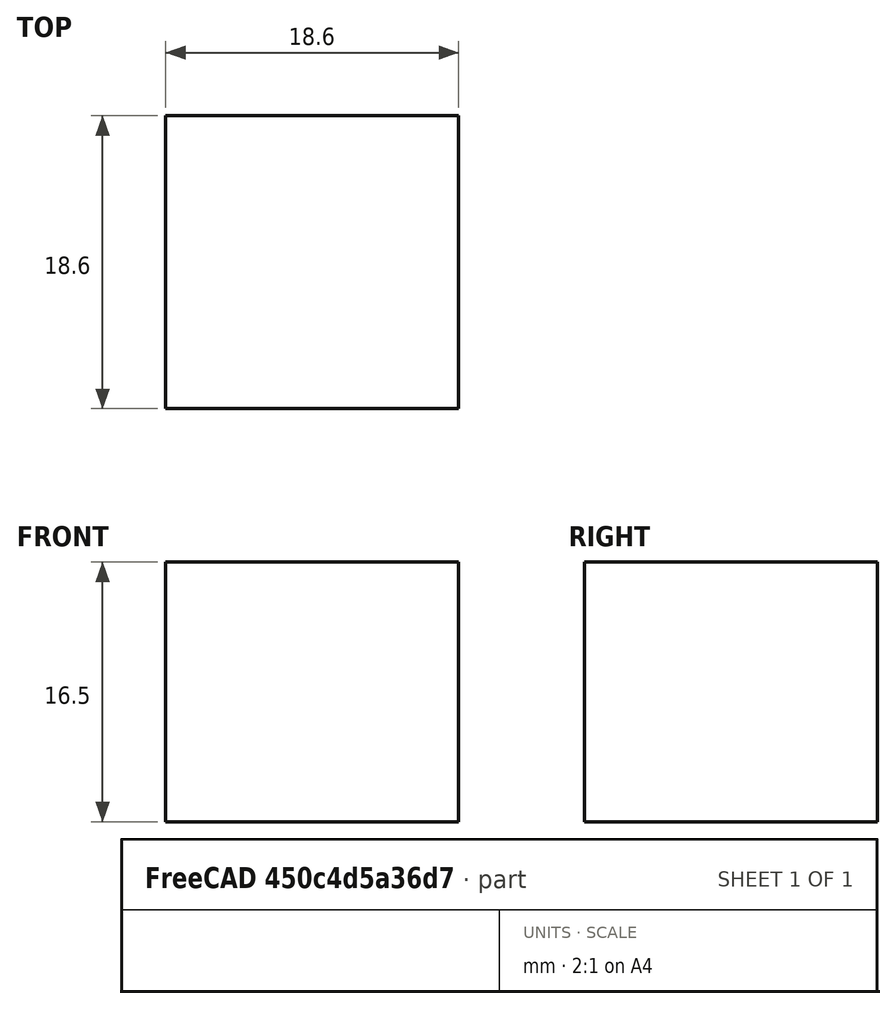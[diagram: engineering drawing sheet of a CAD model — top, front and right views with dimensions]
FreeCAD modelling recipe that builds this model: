
FCSTD DOCUMENT  (FreeCAD 0.15R4671 (Git))
Label: Notched Center Square
License: All rights reserved
LicenseURL: http://en.wikipedia.org/wiki/All_rights_reserved
objects: Sketcher::SketchObject×2, PartDesign::Pad×1
note: 4 computed .brp shape members not serialized (recipe doc carries the construction recipe); baked Part::Feature solids carry a one-line shape summary decoded from their .brp

FEATURE [Sketcher::SketchObject] Sketch
  sketch-geometry (4):
    g0: LineSegment StartX=-9.3 StartY=9.3 StartZ=0 EndX=9.3 EndY=9.3 EndZ=0
    g1: LineSegment StartX=9.3 StartY=9.3 StartZ=0 EndX=9.3 EndY=-9.3 EndZ=0
    g2: LineSegment StartX=9.3 StartY=-9.3 StartZ=0 EndX=-9.3 EndY=-9.3 EndZ=0
    g3: LineSegment StartX=-9.3 StartY=-9.3 StartZ=0 EndX=-9.3 EndY=9.3 EndZ=0
  constraints (12):
    c: Coincident(g0,g1)
    c: Coincident(g1,g2)
    c: Coincident(g2,g3)
    c: Coincident(g3,g0)
    c: Horizontal(g0)
    c: Horizontal(g2)
    c: Vertical(g1)
    c: Vertical(g3)
    c: Symmetric(g0,g0,g-2)
    c: Symmetric(g0,g2,g-1)
    c: Equal(g3,g0)
    c: Distance(g0) = 18.6
FEATURE [PartDesign::Pad] Pad
  Length = 16.5
  Length2 = 100
  Sketch = -> Sketch
  Type = 0
FEATURE [Sketcher::SketchObject] Sketch001
  ExternalGeometry = -> [Pad]
  Placement = pos=(0,-9.3,0) rot=(1,0,0;1.5708rad)
  Support = -> Pad [Face3]
  sketch-geometry (1):
    g0: Circle CenterX=0 CenterY=32.8721 CenterZ=0 NormalX=0 NormalY=0 NormalZ=1 Radius=18.0771
  constraints (1):
    c: PointOnObject(g0,g-2)
